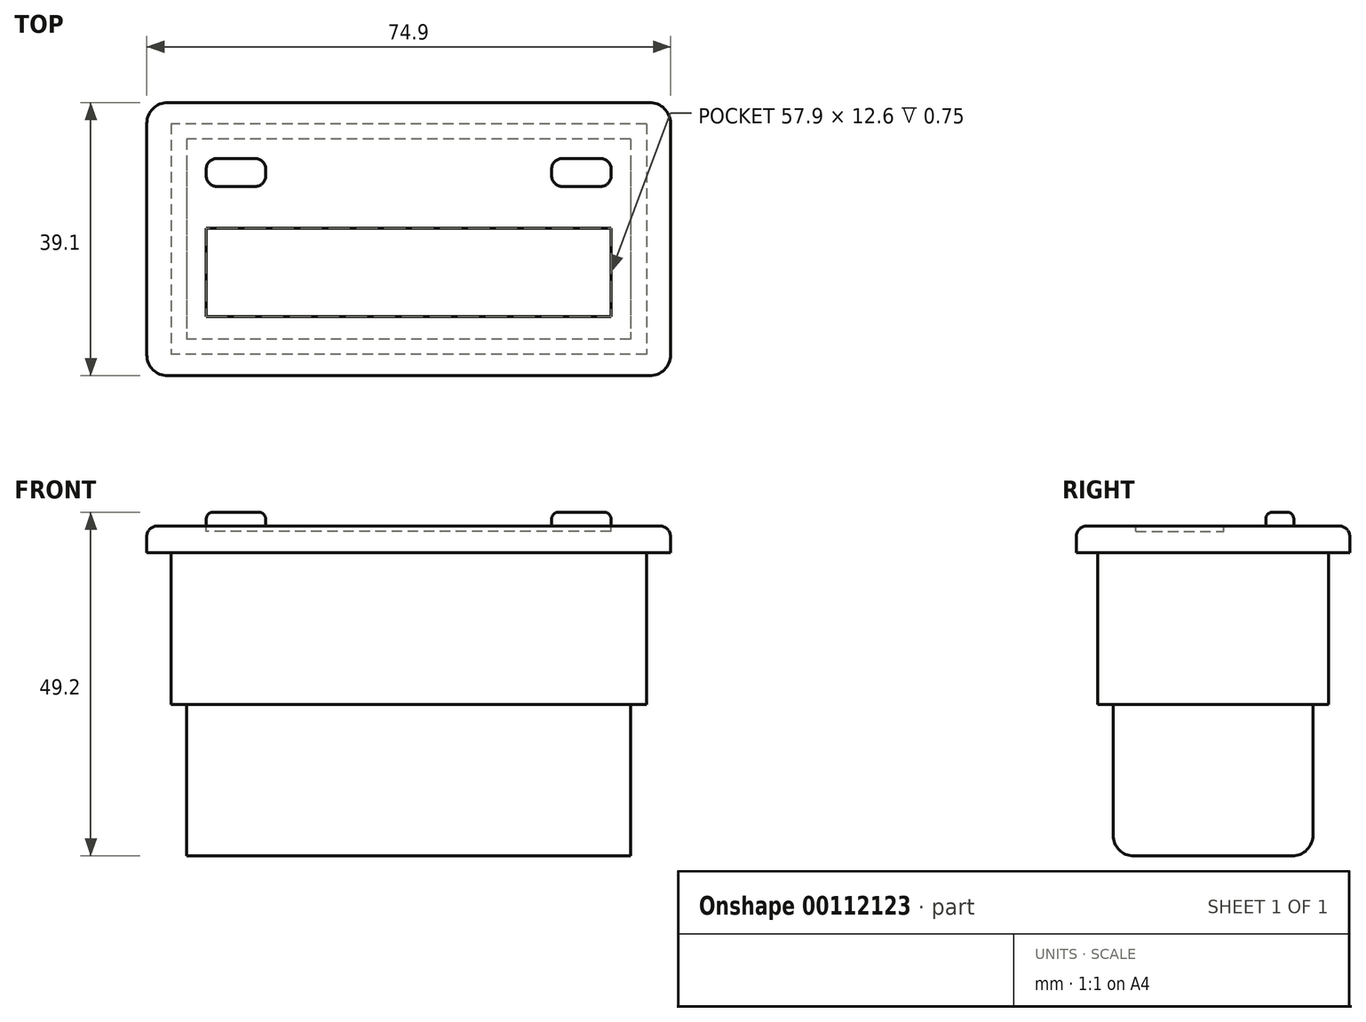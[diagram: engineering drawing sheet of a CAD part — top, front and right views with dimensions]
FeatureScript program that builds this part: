
annotation { "Feature Type Name" : "Feature", "Feature Type Description" : "" }
export const myFeature = defineFeature(function(context is Context, id is Id, definition is map)
    precondition{}
    {
        {
            var Q0;
            Q0=qCreatedBy(makeId("Top.planeOp"),FACE);
            var sketch = newSketch(context, id + "F0", { "sketchPlane" : qUnion([Q0])});
            skLineSegment(sketch, "E0.bottom", {"start": v(34.45, -19.55) * mm, "end": v(-34.45, -19.55) * mm});
            skLineSegment(sketch, "E0.top", {"start": v(34.45, 19.55) * mm, "end": v(-34.45, 19.55) * mm});
            skLineSegment(sketch, "E0.left", {"start": v(37.45, -16.55) * mm, "end": v(37.45, 16.55) * mm});
            skLineSegment(sketch, "E0.right", {"start": v(-37.45, -16.55) * mm, "end": v(-37.45, 16.55) * mm});
            skPoint(sketch, "E0.middle", {"position": v(0, 0) * mm});
            skPoint(sketch, "E1.visualSharp", {"position": v(-37.45, 19.55) * mm});
            skArc(sketch, "E1.filletArc", {"start": v(-34.45, 19.55) * mm, "mid": v(-36.57, 18.67) * mm, "end": v(-37.45, 16.55) * mm});
            skPoint(sketch, "E2.visualSharp", {"position": v(37.45, 19.55) * mm});
            skArc(sketch, "E2.filletArc", {"start": v(37.45, 16.55) * mm, "mid": v(36.57, 18.67) * mm, "end": v(34.45, 19.55) * mm});
            skPoint(sketch, "E3.visualSharp", {"position": v(37.45, -19.55) * mm});
            skArc(sketch, "E3.filletArc", {"start": v(34.45, -19.55) * mm, "mid": v(36.57, -18.67) * mm, "end": v(37.45, -16.55) * mm});
            skPoint(sketch, "E4.visualSharp", {"position": v(-37.45, -19.55) * mm});
            skArc(sketch, "E4.filletArc", {"start": v(-37.45, -16.55) * mm, "mid": v(-36.57, -18.67) * mm, "end": v(-34.45, -19.55) * mm});
            skSolve(sketch);
        }
        {
            var Q0;
            Q0=makeQuery(id+"F0.imprint","IMPRINT",FACE,{"disambiguationData":[TD([[makeQuery(id+"F0.imprint","IMPRINT",EDGE,{"derivedFrom":sQuery(id+"F0.wireOp",EDGE,"E0.bottom")}),-1.0]])]});
            extrude(context, id + "F1", {"entities" : qUnion([Q0]), "depth" : 3.8 * mm});
        }
        {
            var Q0;
            Q0=makeQuery(id+"F1.opExtrude","CAP_FACE",FACE,{"disambiguationData":[OSD([sQuery(id+"F0.wireOp",EDGE,"E0.bottom"),sQuery(id+"F0.wireOp",EDGE,"E0.top"),sQuery(id+"F0.wireOp",EDGE,"E0.left"),sQuery(id+"F0.wireOp",EDGE,"E0.right"),sQuery(id+"F0.wireOp",EDGE,"E1.filletArc"),sQuery(id+"F0.wireOp",EDGE,"E2.filletArc"),sQuery(id+"F0.wireOp",EDGE,"E3.filletArc"),sQuery(id+"F0.wireOp",EDGE,"E4.filletArc")])],"isStart":false});
            fillet(context, id + "F2", {"entities" : qUnion([Q0]), "radius" : 1.5 * mm, "tangentPropagation" : true, "allowEdgeOverflow" : false});
        }
        {
            var Q0;
            Q0=makeQuery(id+"F1.opExtrude","CAP_FACE",FACE,{"disambiguationData":[OSD([sQuery(id+"F0.wireOp",EDGE,"E0.bottom"),sQuery(id+"F0.wireOp",EDGE,"E0.top"),sQuery(id+"F0.wireOp",EDGE,"E0.left"),sQuery(id+"F0.wireOp",EDGE,"E0.right"),sQuery(id+"F0.wireOp",EDGE,"E1.filletArc"),sQuery(id+"F0.wireOp",EDGE,"E2.filletArc"),sQuery(id+"F0.wireOp",EDGE,"E3.filletArc"),sQuery(id+"F0.wireOp",EDGE,"E4.filletArc")])],"isStart":true});
            var sketch = newSketch(context, id + "F3", { "sketchPlane" : qUnion([Q0])});
            skLineSegment(sketch, "E5.bottom", {"start": v(34, -16.5) * mm, "end": v(-34, -16.5) * mm});
            skLineSegment(sketch, "E5.top", {"start": v(34, 16.5) * mm, "end": v(-34, 16.5) * mm});
            skLineSegment(sketch, "E5.left", {"start": v(34, -16.5) * mm, "end": v(34, 16.5) * mm});
            skLineSegment(sketch, "E5.right", {"start": v(-34, -16.5) * mm, "end": v(-34, 16.5) * mm});
            skPoint(sketch, "E5.middle", {"position": v(0, 0) * mm});
            skSolve(sketch);
        }
        {
            var Q0;
            Q0=makeQuery(id+"F3.imprint","IMPRINT",FACE,{"disambiguationData":[TD([[makeQuery(id+"F3.imprint","IMPRINT",EDGE,{"derivedFrom":sQuery(id+"F3.wireOp",EDGE,"E5.bottom")}),-1.0]])]});
            extrude(context, id + "F4", {"entities" : qUnion([Q0]), "operationType" : NewBodyOperationType.ADD, "depth" : 21.7 * mm});
        }
        {
            var Q0;
            Q0=makeQuery(id+"F4.opExtrude","CAP_FACE",FACE,{"disambiguationData":[OSD([sQuery(id+"F3.wireOp",EDGE,"E5.bottom"),sQuery(id+"F3.wireOp",EDGE,"E5.top"),sQuery(id+"F3.wireOp",EDGE,"E5.left"),sQuery(id+"F3.wireOp",EDGE,"E5.right")])],"isStart":false});
            var sketch = newSketch(context, id + "F5", { "sketchPlane" : qUnion([Q0])});
            skLineSegment(sketch, "E6.bottom", {"start": v(31.75, -14.3) * mm, "end": v(-31.75, -14.3) * mm});
            skLineSegment(sketch, "E6.top", {"start": v(31.75, 14.3) * mm, "end": v(-31.75, 14.3) * mm});
            skLineSegment(sketch, "E6.left", {"start": v(31.75, -14.3) * mm, "end": v(31.75, 14.3) * mm});
            skLineSegment(sketch, "E6.right", {"start": v(-31.75, -14.3) * mm, "end": v(-31.75, 14.3) * mm});
            skPoint(sketch, "E6.middle", {"position": v(0, 0) * mm});
            skSolve(sketch);
        }
        {
            var Q0;
            Q0=makeQuery(id+"F5.imprint","IMPRINT",FACE,{"disambiguationData":[TD([[makeQuery(id+"F5.imprint","IMPRINT",EDGE,{"derivedFrom":sQuery(id+"F5.wireOp",EDGE,"E6.bottom")}),-1.0]])]});
            extrude(context, id + "F6", {"entities" : qUnion([Q0]), "operationType" : NewBodyOperationType.ADD, "depth" : 21.7 * mm});
        }
        {
            var Q0;
            Q0=makeQuery(id+"F6.opExtrude","CAP_EDGE",EDGE,{"disambiguationData":[OSD([sQuery(id+"F5.wireOp",EDGE,"E6.top")])],"isStart":false});
            var Q1;
            Q1=makeQuery(id+"F6.opExtrude","CAP_EDGE",EDGE,{"disambiguationData":[OSD([sQuery(id+"F5.wireOp",EDGE,"E6.bottom")])],"isStart":false});
            fillet(context, id + "F7", {"entities" : qUnion([Q0, Q1]), "radius" : 3 * mm, "tangentPropagation" : true, "allowEdgeOverflow" : false});
        }
        {
            var Q0;
            Q0=makeQuery(id+"F1.opExtrude","CAP_FACE",FACE,{"disambiguationData":[OSD([sQuery(id+"F0.wireOp",EDGE,"E0.bottom"),sQuery(id+"F0.wireOp",EDGE,"E0.top"),sQuery(id+"F0.wireOp",EDGE,"E0.left"),sQuery(id+"F0.wireOp",EDGE,"E0.right"),sQuery(id+"F0.wireOp",EDGE,"E1.filletArc"),sQuery(id+"F0.wireOp",EDGE,"E2.filletArc"),sQuery(id+"F0.wireOp",EDGE,"E3.filletArc"),sQuery(id+"F0.wireOp",EDGE,"E4.filletArc")])],"isStart":false});
            var sketch = newSketch(context, id + "F8", { "sketchPlane" : qUnion([Q0])});
            skLineSegment(sketch, "E7.bottom", {"start": v(28.95, -11.05) * mm, "end": v(-28.95, -11.05) * mm});
            skLineSegment(sketch, "E7.top", {"start": v(28.95, 1.55) * mm, "end": v(-28.95, 1.55) * mm});
            skLineSegment(sketch, "E7.left", {"start": v(28.95, -11.05) * mm, "end": v(28.95, 1.55) * mm});
            skLineSegment(sketch, "E7.right", {"start": v(-28.95, -11.05) * mm, "end": v(-28.95, 1.55) * mm});
            skLineSegment(sketch, "E8.bottom", {"start": v(27.45, 7.55) * mm, "end": v(21.95, 7.55) * mm});
            skLineSegment(sketch, "E8.top", {"start": v(27.45, 11.55) * mm, "end": v(21.95, 11.55) * mm});
            skLineSegment(sketch, "E8.left", {"start": v(28.95, 9.05) * mm, "end": v(28.95, 10.05) * mm});
            skLineSegment(sketch, "E8.right", {"start": v(20.45, 9.05) * mm, "end": v(20.45, 10.05) * mm});
            skPoint(sketch, "E9.visualSharp", {"position": v(28.95, 7.55) * mm});
            skArc(sketch, "E9.filletArc", {"start": v(27.45, 7.55) * mm, "mid": v(28.51, 7.99) * mm, "end": v(28.95, 9.05) * mm});
            skPoint(sketch, "E10.visualSharp", {"position": v(20.45, 7.55) * mm});
            skArc(sketch, "E10.filletArc", {"start": v(20.45, 9.05) * mm, "mid": v(20.89, 7.99) * mm, "end": v(21.95, 7.55) * mm});
            skPoint(sketch, "E11.visualSharp", {"position": v(20.45, 11.55) * mm});
            skArc(sketch, "E11.filletArc", {"start": v(21.95, 11.55) * mm, "mid": v(20.89, 11.11) * mm, "end": v(20.45, 10.05) * mm});
            skPoint(sketch, "E12.visualSharp", {"position": v(28.95, 11.55) * mm});
            skArc(sketch, "E12.filletArc", {"start": v(28.95, 10.05) * mm, "mid": v(28.51, 11.11) * mm, "end": v(27.45, 11.55) * mm});
            skLineSegment(sketch, "E13.MirrorCS", {"start": v(-20.45, 9.05) * mm, "end": v(-20.45, 10.05) * mm});
            skLineSegment(sketch, "E14.MirrorCS", {"start": v(-28.95, 9.05) * mm, "end": v(-28.95, 10.05) * mm});
            skPoint(sketch, "E15.MirrorP", {"position": v(-20.45, 7.55) * mm});
            skPoint(sketch, "E16.MirrorP", {"position": v(-28.95, 7.55) * mm});
            skLineSegment(sketch, "E17.MirrorCS", {"start": v(-27.45, 11.55) * mm, "end": v(-21.95, 11.55) * mm});
            skPoint(sketch, "E18.MirrorP", {"position": v(-20.45, 11.55) * mm});
            skArc(sketch, "E19.MirrorCS", {"start": v(-21.95, 11.55) * mm, "mid": v(-20.89, 11.11) * mm, "end": v(-20.45, 10.05) * mm});
            skArc(sketch, "E20.MirrorCS", {"start": v(-28.95, 10.05) * mm, "mid": v(-28.51, 11.11) * mm, "end": v(-27.45, 11.55) * mm});
            skArc(sketch, "E21.MirrorCS", {"start": v(-20.45, 9.05) * mm, "mid": v(-20.89, 7.99) * mm, "end": v(-21.95, 7.55) * mm});
            skArc(sketch, "E22.MirrorCS", {"start": v(-27.45, 7.55) * mm, "mid": v(-28.51, 7.99) * mm, "end": v(-28.95, 9.05) * mm});
            skPoint(sketch, "E23.MirrorP", {"position": v(-28.95, 11.55) * mm});
            skLineSegment(sketch, "E24.MirrorCS", {"start": v(-27.45, 7.55) * mm, "end": v(-21.95, 7.55) * mm});
            skSolve(sketch);
        }
        {
            var Q0;
            Q0=makeQuery(id+"F8.imprint","IMPRINT",FACE,{"disambiguationData":[TD([[makeQuery(id+"F8.imprint","IMPRINT",EDGE,{"derivedFrom":sQuery(id+"F8.wireOp",EDGE,"E8.bottom")}),-1.0]])]});
            var Q1;
            Q1=makeQuery(id+"F8.imprint","IMPRINT",FACE,{"disambiguationData":[TD([[makeQuery(id+"F8.imprint","IMPRINT",EDGE,{"derivedFrom":sQuery(id+"F8.wireOp",EDGE,"E13.MirrorCS")}),1.0]])]});
            extrude(context, id + "F9", {"entities" : qUnion([Q0, Q1]), "operationType" : NewBodyOperationType.ADD, "depth" : 2 * mm});
        }
        {
            var Q0;
            Q0=makeQuery(id+"F9.opExtrude","CAP_FACE",FACE,{"disambiguationData":[OSD([sQuery(id+"F8.wireOp",EDGE,"E8.bottom"),sQuery(id+"F8.wireOp",EDGE,"E8.top"),sQuery(id+"F8.wireOp",EDGE,"E8.left"),sQuery(id+"F8.wireOp",EDGE,"E8.right"),sQuery(id+"F8.wireOp",EDGE,"E9.filletArc"),sQuery(id+"F8.wireOp",EDGE,"E10.filletArc"),sQuery(id+"F8.wireOp",EDGE,"E11.filletArc"),sQuery(id+"F8.wireOp",EDGE,"E12.filletArc")])],"isStart":false});
            var Q1;
            Q1=makeQuery(id+"F9.opExtrude","CAP_FACE",FACE,{"disambiguationData":[OSD([sQuery(id+"F8.wireOp",EDGE,"E13.MirrorCS"),sQuery(id+"F8.wireOp",EDGE,"E14.MirrorCS"),sQuery(id+"F8.wireOp",EDGE,"E17.MirrorCS"),sQuery(id+"F8.wireOp",EDGE,"E19.MirrorCS"),sQuery(id+"F8.wireOp",EDGE,"E20.MirrorCS"),sQuery(id+"F8.wireOp",EDGE,"E21.MirrorCS"),sQuery(id+"F8.wireOp",EDGE,"E22.MirrorCS"),sQuery(id+"F8.wireOp",EDGE,"E24.MirrorCS")])],"isStart":false});
            fillet(context, id + "F10", {"entities" : qUnion([Q0, Q1]), "radius" : 1 * mm, "tangentPropagation" : true, "allowEdgeOverflow" : false});
        }
        {
            var Q0;
            Q0=makeQuery(id+"F8.imprint","IMPRINT",FACE,{"disambiguationData":[TD([[makeQuery(id+"F8.imprint","IMPRINT",EDGE,{"derivedFrom":sQuery(id+"F8.wireOp",EDGE,"E7.bottom")}),-1.0]])]});
            extrude(context, id + "F11", {"entities" : qUnion([Q0]), "operationType" : NewBodyOperationType.REMOVE, "oppositeDirection" : true, "depth" : 0.75 * mm});
        }
    });
